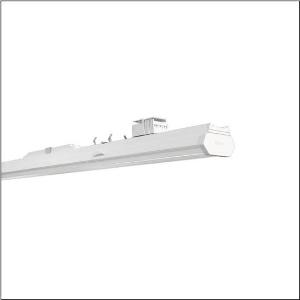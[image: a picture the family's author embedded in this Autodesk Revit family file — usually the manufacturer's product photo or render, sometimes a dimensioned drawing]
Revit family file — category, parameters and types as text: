
# Revit family: licross_r__21_protected_ho_52td12dn4e5m_4ef7
name_source: partatom
category: Lighting Fixtures
units: mm (PartAtom-declared; Revit-internal decimal feet)

## family parameters
Cut with Voids When Loaded = No
Host = Face
Light Source = No
Part Type = Normal
Room Calculation Point = No
Round Connector Dimension = Use Diameter
Shared = No

## types (1)
- --- (1 x LED, 14690 lm, 84.9 W, 4000K)
    Apparent Load = 85 VA
    CIE Flux Codes = 70 91 97 98 100
    Color Rendering = 80
    Color Temperature = 4000K
    Default Elevation = 1800 mm
    Description = Licross® 21 Protected HO, luminaire insert, of sheet steel, galvanised, coil coated, white, length: 1.500mm, width: 90mm, height: 103mm, LED rated luminous flux: 14.690lm, light colour: 840, SDCM (Standard Deviation of Colour Matching)MacAdam ≤ 3 SDCM (initial), control gear: DALI 2, with plug, 5-pole, with phase selection, mains connection: 220..240V, AC, 50/60Hz, rated input power: 85W, internal wiring halogen-free, primary light control with lens, of plastic, primary optical cover: cover, of PMMA, light emission: direct distribution, primary light characteristic: symmetric, protection rating (complete): IP54, insulation class (complete): insulation class I (protective earthing), certification: CE, ENEC, VDE, UKCA, protection symbol: D if used in an environment with non-conductive dust loads with corresponding accessories, impact resistance: IK06, permissible ambient temperature for indoor applications: -25..+35°C, corresponds to IFS (International Featured Standards) requirements for safety and quality in the food industry, reducing of maximum allowable ambient temperature of 5°C with ceiling mounting, LABS conformity tested according to VDMA 24364:2018-05, packaging unit: 1 piece
    Height = 92 mm
    Lamp = 1 x LED
    Lamp Light Flux = 14690 lm
    Lamp Power = 84.9 W
    Lamp count = 1
    Length = 1500 mm
    Luminous efficacy = 173 lm/W
    Manufacturer = Siteco
    ModVariant = No
    Model = 52TD12DN4E5M
    Mounting Place = Ceiling
    Mounting Type = Pendant
    Number of Poles = 1
    OnlyDefault = Yes
    Power Factor = 1
    Product Name = Licross® 21 Protected HO
    Product group = luminaire insert | ceiling pendant
    ProductGroupID = 901
    Protection Class = Protection class I
    Protection Degree = IP 54
    RLX_Detail_Level = 1
    RLX_Emergency_Light_Flux = 0 lm
    RLX_Emergency_Type = 0
    RLX_Emergency_Type_DB = No
    RlxData = <blob elided: 24541 chars, md5=876dee2e>
    Socket = socket
    Standby Power = 0 W
    System Light Flux = 14690 lm
    System Power = 85 W
    Type Comments = factory setting: luminous flux: 100 % | dim-lin: 254 | 484 mA
    Type Image = l_1256148.jpg
    URL = http://relux.com
    VarID = @adj_132959
    Voltage = 0 V
    Weight = 0.00 kg
    Width = 88 mm

## geometry (parser evidence)
native form markers: Blend x4, Sweep x10
no freeform markers — native parametric forms only
